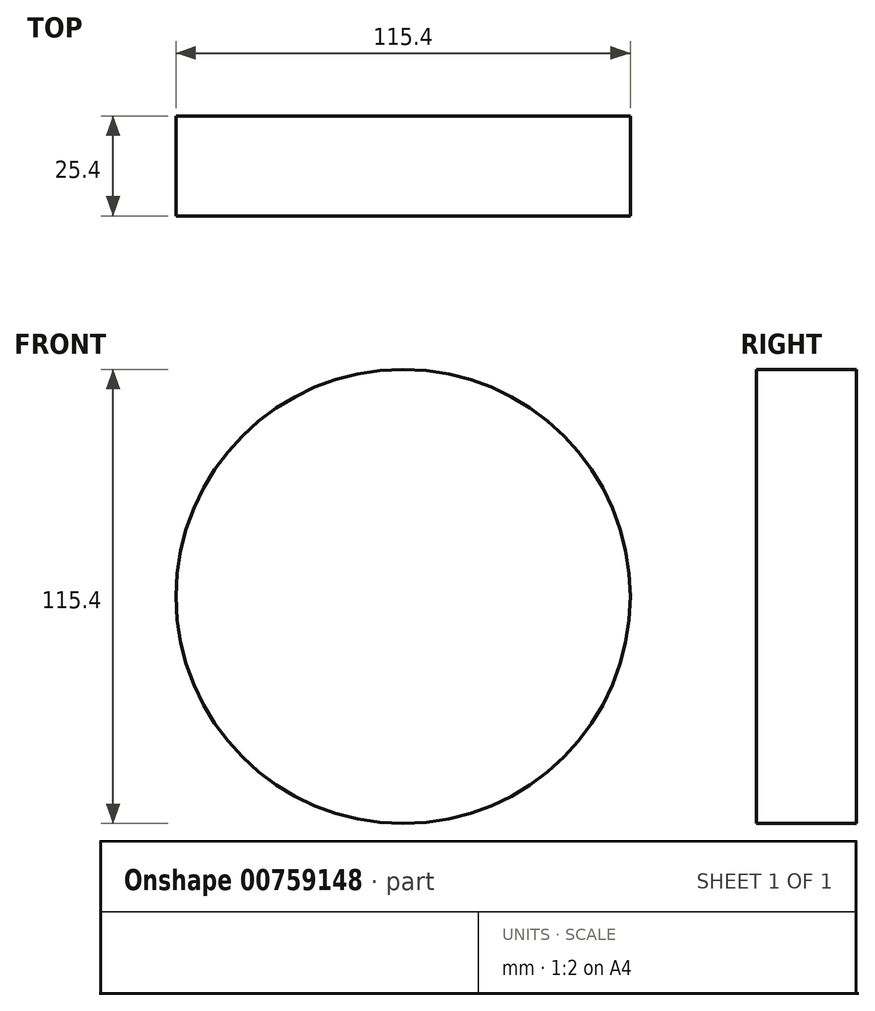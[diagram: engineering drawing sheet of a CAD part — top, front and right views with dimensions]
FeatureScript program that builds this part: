
annotation { "Feature Type Name" : "Feature", "Feature Type Description" : "" }
export const myFeature = defineFeature(function(context is Context, id is Id, definition is map)
    precondition{}
    {
        {
            var Q0;
            Q0=qCreatedBy(makeId("Front.planeOp"),FACE);
            var sketch = newSketch(context, id + "F0", { "sketchPlane" : qUnion([Q0])});
            skCircle(sketch, "E0", {"center": v(0, 0) * mm, "radius": 57.7 * mm});
            skSolve(sketch);
        }
        {
            var Q0;
            Q0=sQuery(id+"F0.wireOp",EDGE,"E0");
            extrude(context, id + "F1", {"bodyType" : ToolBodyType.SURFACE, "surfaceEntities" : qUnion([Q0]), "depth" : 25.4 * mm, "offsetDistance" : 25.4 * mm});
        }
    });
